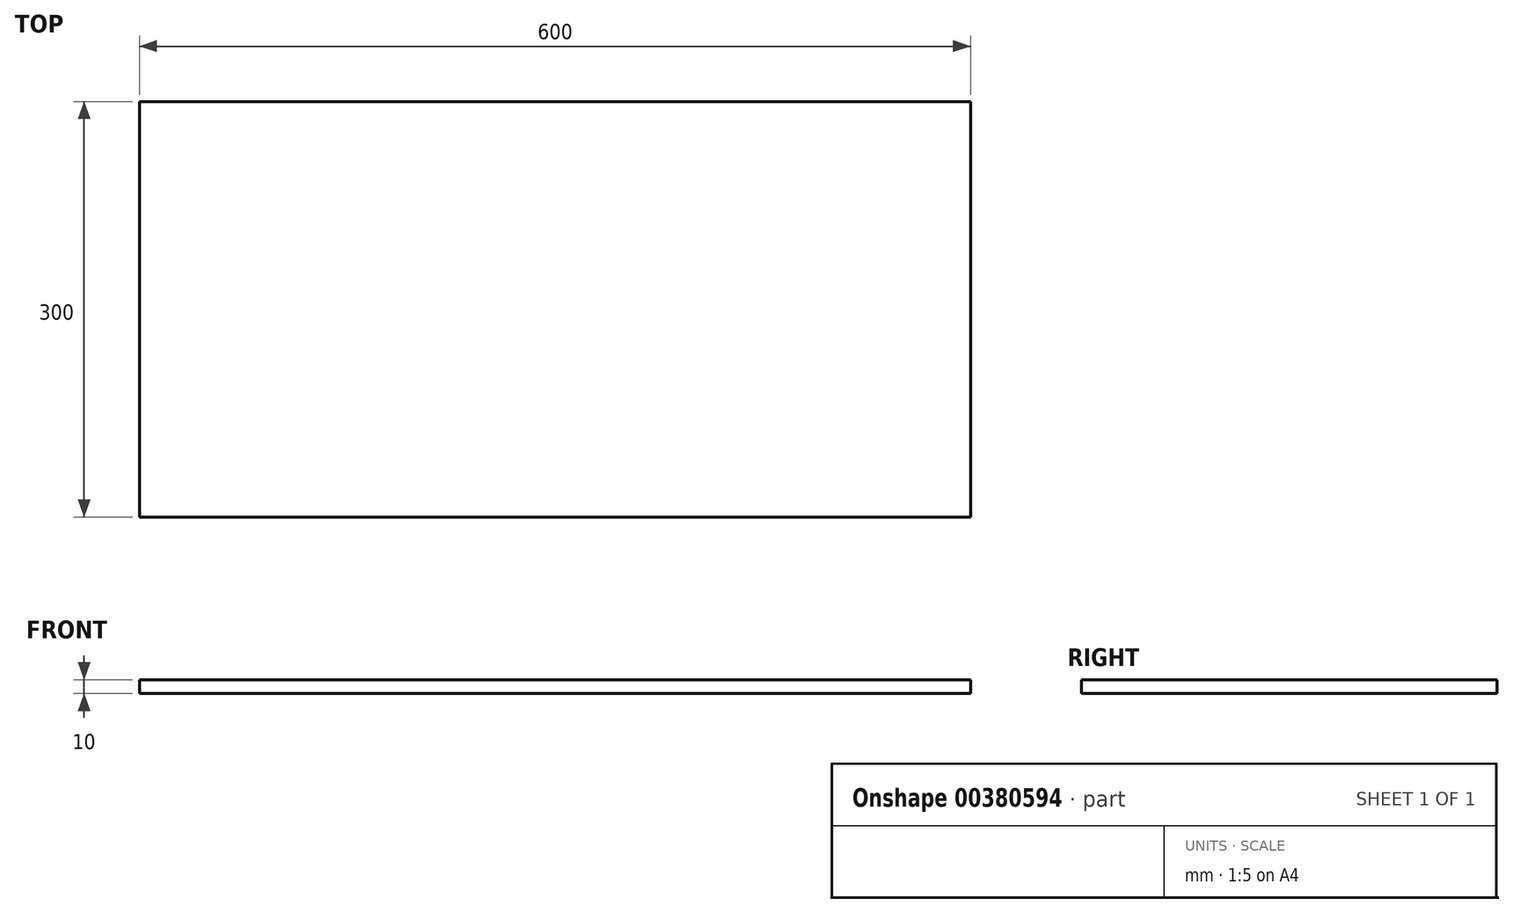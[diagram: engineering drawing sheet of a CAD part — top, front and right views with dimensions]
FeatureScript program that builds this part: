
annotation { "Feature Type Name" : "Feature", "Feature Type Description" : "" }
export const myFeature = defineFeature(function(context is Context, id is Id, definition is map)
    precondition{}
    {
        {
            var Q0;
            Q0=qCreatedBy(makeId("Top.planeOp"),FACE);
            var sketch = newSketch(context, id + "F0", { "sketchPlane" : qUnion([Q0])});
            skLineSegment(sketch, "E0.bottom", {"start": v(300, -150) * mm, "end": v(-300, -150) * mm});
            skLineSegment(sketch, "E0.top", {"start": v(300, 150) * mm, "end": v(-300, 150) * mm});
            skLineSegment(sketch, "E0.left", {"start": v(300, -150) * mm, "end": v(300, 150) * mm});
            skLineSegment(sketch, "E0.right", {"start": v(-300, -150) * mm, "end": v(-300, 150) * mm});
            skPoint(sketch, "E0.middle", {"position": v(0, 0) * mm});
            skSolve(sketch);
        }
        {
            var Q0;
            Q0 = qSketchRegion(id + "F0", true);
            extrude(context, id + "F1", {"entities" : qUnion([Q0]), "depth" : 10 * mm});
        }
    });
